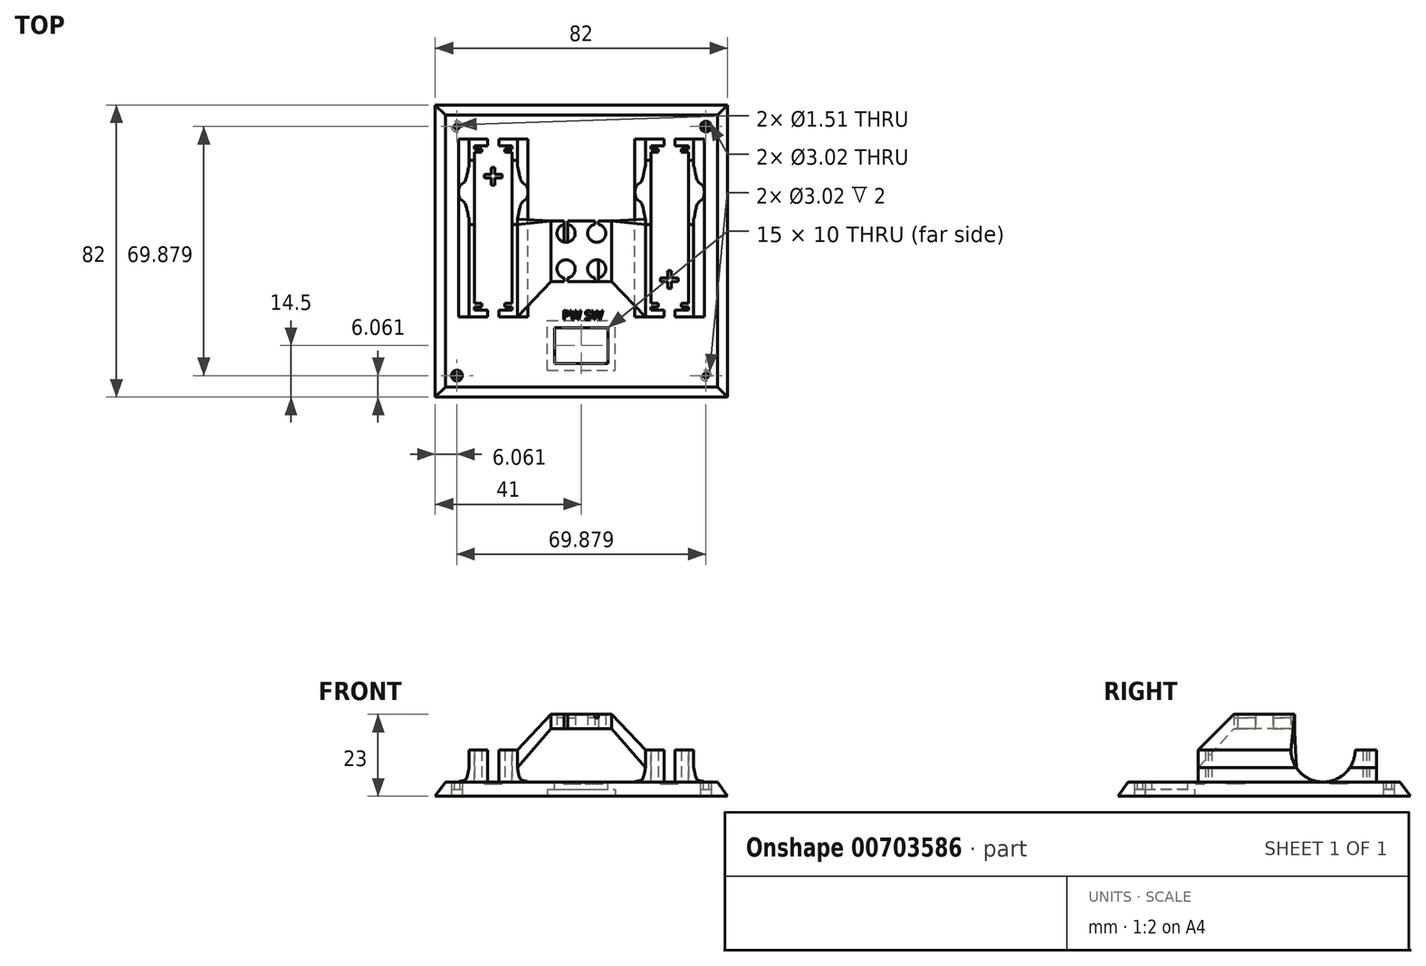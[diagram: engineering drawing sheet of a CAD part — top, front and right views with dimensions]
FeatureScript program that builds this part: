
annotation { "Feature Type Name" : "Feature", "Feature Type Description" : "" }
export const myFeature = defineFeature(function(context is Context, id is Id, definition is map)
    precondition{}
    {
        {
            assignVariable(context, id + "F0", {"name" : "Hollow", "anyValue" : 82});
        }
        {
            assignVariable(context, id + "F1", {"name" : "BaseThicknes", "anyValue" : 4});
        }
        {
            var Q0;
            Q0=qCreatedBy(makeId("Top.planeOp"),FACE);
            cPlane(context, id + "F2", {"entities" : qUnion([Q0]), "cplaneType" : CPlaneType.OFFSET, "offset" : (sqrt((sqrt((getVariable(context, 'Hollow') * getVariable(context, 'Hollow')) - ((getVariable(context, 'Hollow') / 2) * (getVariable(context, 'Hollow') / 2)))) * (sqrt((getVariable(context, 'Hollow') * getVariable(context, 'Hollow')) - ((getVariable(context, 'Hollow') / 2) * (getVariable(context, 'Hollow') / 2)))) - ((getVariable(context, 'Hollow') / 2) * (getVariable(context, 'Hollow') / 2)))) * mm, "width" : 150 * mm, "height" : 150 * mm});
        }
        {
            var Q0;
            Q0=qCreatedBy(id+"F2.planeOp",FACE);
            var sketch = newSketch(context, id + "F3", { "sketchPlane" : qUnion([Q0])});
            skPoint(sketch, "E0", {"position": v(0, 0) * mm});
            skSolve(sketch);
        }
        {
            var Q0;
            Q0=qCreatedBy(makeId("Top.planeOp"),FACE);
            var sketch = newSketch(context, id + "F4", { "sketchPlane" : qUnion([Q0])});
            skLineSegment(sketch, "E1.bottom", {"start": v(-41, 41) * mm, "end": v(41, 41) * mm});
            skLineSegment(sketch, "E1.top", {"start": v(-41, -41) * mm, "end": v(41, -41) * mm});
            skLineSegment(sketch, "E1.left", {"start": v(-41, 41) * mm, "end": v(-41, -41) * mm});
            skLineSegment(sketch, "E1.right", {"start": v(41, 41) * mm, "end": v(41, -41) * mm});
            skSolve(sketch);
        }
        {
            var Q0;
            Q0=qSketchRegion(id+"F4",true);
            extrude(context, id + "F5", {"entities" : qUnion([Q0]), "depth" : (getVariable(context, 'BaseThicknes')) * mm, "offsetDistance" : 25 * mm});
        }
        {
            var Q1;
            Q1=makeQuery(id+"F5.opExtrude","CAP_FACE",FACE,{"disambiguationData":[OSD([sQuery(id+"F4.wireOp",EDGE,"E1.bottom"),sQuery(id+"F4.wireOp",EDGE,"E1.top"),sQuery(id+"F4.wireOp",EDGE,"E1.left"),sQuery(id+"F4.wireOp",EDGE,"E1.right")])],"isStart":true});
            var Q2;
            Q2=sQuery(id+"F3.wireOp",VERTEX,"E0");
            loft(context, id + "F6", {"operationType" : NewBodyOperationType.INTERSECT, "sheetProfilesArray" : [{ "sheetProfileEntities" : qUnion([Q1]) }, { "sheetProfileEntities" : qUnion([Q2]) }]});
        }
        {
            var Q0;
            Q0=makeQuery(id+"F5.opExtrude","CAP_FACE",FACE,{"disambiguationData":[OSD([sQuery(id+"F4.wireOp",EDGE,"E1.bottom"),sQuery(id+"F4.wireOp",EDGE,"E1.top"),sQuery(id+"F4.wireOp",EDGE,"E1.left"),sQuery(id+"F4.wireOp",EDGE,"E1.right")])],"isStart":true});
            var sketch = newSketch(context, id + "F7", { "sketchPlane" : qUnion([Q0])});
            skCircle(sketch, "E2", {"center": v(-34.94, -34.94) * mm, "radius": 0.76 * mm});
            skCircle(sketch, "E3.MirrorC", {"center": v(34.94, -34.94) * mm, "radius": 0.76 * mm});
            skCircle(sketch, "E4.MirrorC", {"center": v(34.94, 34.94) * mm, "radius": 0.76 * mm});
            skCircle(sketch, "E5.MirrorC", {"center": v(-34.94, 34.94) * mm, "radius": 0.76 * mm});
            skCircle(sketch, "E6", {"center": v(-34.94, -34.94) * mm, "radius": 1.51 * mm});
            skCircle(sketch, "E7.MirrorC", {"center": v(-34.94, 34.94) * mm, "radius": 1.51 * mm});
            skCircle(sketch, "E8.MirrorC", {"center": v(34.94, -34.94) * mm, "radius": 1.51 * mm});
            skCircle(sketch, "E9.MirrorC", {"center": v(34.94, 34.94) * mm, "radius": 1.51 * mm});
            skSolve(sketch);
        }
        {
            var Q0;
            Q0=makeQuery(id+"F7.imprint","IMPRINT",FACE,{"disambiguationData":[TD([[makeQuery(id+"F7.imprint","IMPRINT",EDGE,{"derivedFrom":sQuery(id+"F7.wireOp",EDGE,"E2")}),1.0]])]});
            var Q1;
            Q1=makeQuery(id+"F7.imprint","IMPRINT",FACE,{"disambiguationData":[TD([[makeQuery(id+"F7.imprint","IMPRINT",EDGE,{"derivedFrom":sQuery(id+"F7.wireOp",EDGE,"E5.MirrorC")}),-1.0]])]});
            var Q2;
            Q2=makeQuery(id+"F7.imprint","IMPRINT",FACE,{"disambiguationData":[TD([[makeQuery(id+"F7.imprint","IMPRINT",EDGE,{"derivedFrom":sQuery(id+"F7.wireOp",EDGE,"E4.MirrorC")}),1.0]])]});
            var Q3;
            Q3=makeQuery(id+"F7.imprint","IMPRINT",FACE,{"disambiguationData":[TD([[makeQuery(id+"F7.imprint","IMPRINT",EDGE,{"derivedFrom":sQuery(id+"F7.wireOp",EDGE,"E3.MirrorC")}),-1.0]])]});
            extrude(context, id + "F8", {"entities" : qUnion([Q0, Q1, Q2, Q3]), "operationType" : NewBodyOperationType.REMOVE, "oppositeDirection" : true, "depth" : 25 * mm, "offsetDistance" : 25 * mm});
        }
        {
            var Q0;
            Q0=makeQuery(id+"F7.imprint","IMPRINT",FACE,{"disambiguationData":[TD([[makeQuery(id+"F7.imprint","IMPRINT",EDGE,{"derivedFrom":sQuery(id+"F7.wireOp",EDGE,"E5.MirrorC")}),1.0]])]});
            var Q1;
            Q1=makeQuery(id+"F7.imprint","IMPRINT",FACE,{"disambiguationData":[TD([[makeQuery(id+"F7.imprint","IMPRINT",EDGE,{"derivedFrom":sQuery(id+"F7.wireOp",EDGE,"E4.MirrorC")}),-1.0]])]});
            var Q2;
            Q2=makeQuery(id+"F7.imprint","IMPRINT",FACE,{"disambiguationData":[TD([[makeQuery(id+"F7.imprint","IMPRINT",EDGE,{"derivedFrom":sQuery(id+"F7.wireOp",EDGE,"E2")}),-1.0]])]});
            var Q3;
            Q3=makeQuery(id+"F7.imprint","IMPRINT",FACE,{"disambiguationData":[TD([[makeQuery(id+"F7.imprint","IMPRINT",EDGE,{"derivedFrom":sQuery(id+"F7.wireOp",EDGE,"E3.MirrorC")}),1.0]])]});
            extrude(context, id + "F9", {"entities" : qUnion([Q0, Q1, Q2, Q3]), "operationType" : NewBodyOperationType.REMOVE, "oppositeDirection" : true, "depth" : 2 * mm, "offsetDistance" : 25 * mm});
        }
        {
            var Q0;
            Q0=makeQuery(id+"F5.opExtrude","CAP_FACE",FACE,{"disambiguationData":[OSD([sQuery(id+"F4.wireOp",EDGE,"E1.bottom"),sQuery(id+"F4.wireOp",EDGE,"E1.top"),sQuery(id+"F4.wireOp",EDGE,"E1.left"),sQuery(id+"F4.wireOp",EDGE,"E1.right")])],"isStart":false});
            var sketch = newSketch(context, id + "F10", { "sketchPlane" : qUnion([Q0])});
            skLineSegment(sketch, "E10.bottom", {"start": v(-30, 29.5) * mm, "end": v(-26.3, 29.5) * mm});
            skLineSegment(sketch, "E10.top", {"start": v(-30, -16.5) * mm, "end": v(-26.3, -16.5) * mm});
            skLineSegment(sketch, "E10.left", {"start": v(-30, 29.5) * mm, "end": v(-30, -16.5) * mm});
            skLineSegment(sketch, "E10.right", {"start": v(-19.5, 29.5) * mm, "end": v(-19.5, -16.5) * mm});
            skLineSegment(sketch, "E11.bottom", {"start": v(-31.5, 31.5) * mm, "end": v(-26.3, 31.5) * mm});
            skLineSegment(sketch, "E11.top", {"start": v(-31.5, -18.5) * mm, "end": v(-18, -18.5) * mm});
            skLineSegment(sketch, "E11.left", {"start": v(-31.5, 31.5) * mm, "end": v(-31.5, -18.5) * mm});
            skLineSegment(sketch, "E11.right", {"start": v(-18, 31.5) * mm, "end": v(-18, -18.5) * mm});
            skLineSegment(sketch, "E12", {"start": v(-30, 27.7) * mm, "end": v(-28, 27.7) * mm});
            skLineSegment(sketch, "E13", {"start": v(-30, 28.7) * mm, "end": v(-28, 28.7) * mm});
            skLineSegment(sketch, "E14.left", {"start": v(-21.5, 28.7) * mm, "end": v(-21.5, 27.7) * mm});
            skLineSegment(sketch, "E14.right", {"start": v(-28, 28.7) * mm, "end": v(-28, 27.7) * mm});
            skLineSegment(sketch, "E15", {"start": v(-18, 6.5) * mm, "end": v(-31.5, 6.5) * mm, "construction": true});
            skLineSegment(sketch, "E16.trimOffspring", {"start": v(-21.5, 27.7) * mm, "end": v(-19.5, 27.7) * mm});
            skLineSegment(sketch, "E17.trimOffspring", {"start": v(-21.5, 28.7) * mm, "end": v(-19.5, 28.7) * mm});
            skLineSegment(sketch, "E18.MirrorCS", {"start": v(-30, -15.7) * mm, "end": v(-28, -15.7) * mm});
            skLineSegment(sketch, "E19.MirrorCS", {"start": v(-30, -14.7) * mm, "end": v(-28, -14.7) * mm});
            skLineSegment(sketch, "E20.MirrorCS", {"start": v(-21.5, -15.7) * mm, "end": v(-21.5, -14.7) * mm});
            skLineSegment(sketch, "E21.MirrorCS", {"start": v(-21.5, -15.7) * mm, "end": v(-19.5, -15.7) * mm});
            skLineSegment(sketch, "E22.MirrorCS", {"start": v(-21.5, -14.7) * mm, "end": v(-19.5, -14.7) * mm});
            skLineSegment(sketch, "E23.MirrorCS", {"start": v(-28, -15.7) * mm, "end": v(-28, -14.7) * mm});
            skLineSegment(sketch, "E24", {"start": v(-26.3, 31.5) * mm, "end": v(-26.3, 29.5) * mm});
            skLineSegment(sketch, "E25", {"start": v(-23.2, 31.5) * mm, "end": v(-23.2, 29.5) * mm});
            skLineSegment(sketch, "E26.trimOffspring", {"start": v(-23.2, 31.5) * mm, "end": v(-18, 31.5) * mm});
            skLineSegment(sketch, "E27.trimOffspring", {"start": v(-23.2, 29.5) * mm, "end": v(-19.5, 29.5) * mm});
            skLineSegment(sketch, "E28.MirrorCS", {"start": v(-26.3, -18.5) * mm, "end": v(-26.3, -16.5) * mm});
            skLineSegment(sketch, "E29.MirrorCS", {"start": v(-23.2, -18.5) * mm, "end": v(-23.2, -16.5) * mm});
            skLineSegment(sketch, "E30.trimOffspring", {"start": v(-23.2, -16.5) * mm, "end": v(-19.5, -16.5) * mm});
            skLineSegment(sketch, "E31.MirrorCS", {"start": v(21.5, 28.7) * mm, "end": v(21.5, 27.7) * mm});
            skLineSegment(sketch, "E32.MirrorCS", {"start": v(21.5, 28.7) * mm, "end": v(19.5, 28.7) * mm});
            skLineSegment(sketch, "E33.MirrorCS", {"start": v(23.2, 29.5) * mm, "end": v(19.5, 29.5) * mm});
            skLineSegment(sketch, "E34.MirrorCS", {"start": v(23.2, 31.5) * mm, "end": v(23.2, 29.5) * mm});
            skLineSegment(sketch, "E35.MirrorCS", {"start": v(28, -15.7) * mm, "end": v(28, -14.7) * mm});
            skLineSegment(sketch, "E36.MirrorCS", {"start": v(21.5, -15.7) * mm, "end": v(19.5, -15.7) * mm});
            skLineSegment(sketch, "E37.MirrorCS", {"start": v(23.2, -16.5) * mm, "end": v(19.5, -16.5) * mm});
            skLineSegment(sketch, "E38.MirrorCS", {"start": v(30, -15.7) * mm, "end": v(28, -15.7) * mm});
            skLineSegment(sketch, "E39.MirrorCS", {"start": v(21.5, -14.7) * mm, "end": v(19.5, -14.7) * mm});
            skLineSegment(sketch, "E40.MirrorCS", {"start": v(30, 29.5) * mm, "end": v(26.3, 29.5) * mm});
            skLineSegment(sketch, "E41.MirrorCS", {"start": v(30, 28.7) * mm, "end": v(28, 28.7) * mm});
            skLineSegment(sketch, "E42.MirrorCS", {"start": v(30, -16.5) * mm, "end": v(26.3, -16.5) * mm});
            skLineSegment(sketch, "E43.MirrorCS", {"start": v(26.3, 31.5) * mm, "end": v(26.3, 29.5) * mm});
            skLineSegment(sketch, "E44.MirrorCS", {"start": v(21.5, -15.7) * mm, "end": v(21.5, -14.7) * mm});
            skLineSegment(sketch, "E45.MirrorCS", {"start": v(28, 28.7) * mm, "end": v(28, 27.7) * mm});
            skLineSegment(sketch, "E46.MirrorCS", {"start": v(30, -14.7) * mm, "end": v(28, -14.7) * mm});
            skLineSegment(sketch, "E47.MirrorCS", {"start": v(31.5, 31.5) * mm, "end": v(26.3, 31.5) * mm});
            skLineSegment(sketch, "E48.MirrorCS", {"start": v(21.5, 27.7) * mm, "end": v(19.5, 27.7) * mm});
            skLineSegment(sketch, "E49.MirrorCS", {"start": v(23.2, -18.5) * mm, "end": v(23.2, -16.5) * mm});
            skLineSegment(sketch, "E50.MirrorCS", {"start": v(30, 27.7) * mm, "end": v(28, 27.7) * mm});
            skLineSegment(sketch, "E51.MirrorCS", {"start": v(26.3, -18.5) * mm, "end": v(26.3, -16.5) * mm});
            skLineSegment(sketch, "E52.MirrorCS", {"start": v(23.2, 31.5) * mm, "end": v(18, 31.5) * mm});
            skLineSegment(sketch, "E53.MirrorCS", {"start": v(31.5, 31.5) * mm, "end": v(31.5, -18.5) * mm});
            skLineSegment(sketch, "E54.MirrorCS", {"start": v(30, 29.5) * mm, "end": v(30, -16.5) * mm});
            skLineSegment(sketch, "E55.MirrorCS", {"start": v(31.5, -18.5) * mm, "end": v(18, -18.5) * mm});
            skLineSegment(sketch, "E56.MirrorCS", {"start": v(19.5, 29.5) * mm, "end": v(19.5, -16.5) * mm});
            skLineSegment(sketch, "E57.MirrorCS", {"start": v(18, 31.5) * mm, "end": v(18, -18.5) * mm});
            skLineSegment(sketch, "E58.MirrorCS", {"start": v(18, 6.5) * mm, "end": v(31.5, 6.5) * mm, "construction": true});
            skSolve(sketch);
        }
        {
            var Q0;
            {var subQ5=sQuery(id+"F10.wireOp",EDGE,"E33.MirrorCS");Q0=makeQuery(id+"F10.imprint","IMPRINT",FACE,{"disambiguationData":[TD([[makeQuery(id+"F10.imprint","IMPRINT",EDGE,{"derivedFrom":subQ5}),-1.0]])]});}
            var Q1;
            {var subQ6=sQuery(id+"F10.wireOp",EDGE,"E40.MirrorCS");Q1=makeQuery(id+"F10.imprint","IMPRINT",FACE,{"disambiguationData":[TD([[makeQuery(id+"F10.imprint","IMPRINT",EDGE,{"derivedFrom":subQ6}),-1.0]])]});}
            var Q2;
            Q2=makeQuery(id+"F10.imprint","IMPRINT",FACE,{"disambiguationData":[TD([[makeQuery(id+"F10.imprint","IMPRINT",EDGE,{"derivedFrom":sQuery(id+"F10.wireOp",EDGE,"E31.MirrorCS")}),-1.0]])]});
            var Q3;
            {var subQ0=sQuery(id+"F10.wireOp",EDGE,"E41.MirrorCS");Q3=makeQuery(id+"F10.imprint","IMPRINT",FACE,{"disambiguationData":[TD([[makeQuery(id+"F10.imprint","IMPRINT",EDGE,{"derivedFrom":subQ0}),1.0]])]});}
            var Q4;
            {var subQ0=sQuery(id+"F10.wireOp",EDGE,"E36.MirrorCS");Q4=makeQuery(id+"F10.imprint","IMPRINT",FACE,{"disambiguationData":[TD([[makeQuery(id+"F10.imprint","IMPRINT",EDGE,{"derivedFrom":subQ0}),-1.0]])]});}
            var Q5;
            Q5=makeQuery(id+"F10.imprint","IMPRINT",FACE,{"disambiguationData":[TD([[makeQuery(id+"F10.imprint","IMPRINT",EDGE,{"derivedFrom":sQuery(id+"F10.wireOp",EDGE,"E35.MirrorCS")}),-1.0]])]});
            var Q6;
            Q6=makeQuery(id+"F10.imprint","IMPRINT",FACE,{"disambiguationData":[TD([[makeQuery(id+"F10.imprint","IMPRINT",EDGE,{"derivedFrom":sQuery(id+"F10.wireOp",EDGE,"E20.MirrorCS")}),-1.0]])]});
            var Q7;
            {var subQ0=sQuery(id+"F10.wireOp",EDGE,"E18.MirrorCS");Q7=makeQuery(id+"F10.imprint","IMPRINT",FACE,{"disambiguationData":[TD([[makeQuery(id+"F10.imprint","IMPRINT",EDGE,{"derivedFrom":subQ0}),1.0]])]});}
            var Q8;
            {var subQ6=sQuery(id+"F10.wireOp",EDGE,"E10.bottom");Q8=makeQuery(id+"F10.imprint","IMPRINT",FACE,{"disambiguationData":[TD([[makeQuery(id+"F10.imprint","IMPRINT",EDGE,{"derivedFrom":subQ6}),1.0]])]});}
            var Q9;
            {var subQ0=sQuery(id+"F10.wireOp",EDGE,"E11.right");Q9=makeQuery(id+"F10.imprint","IMPRINT",FACE,{"disambiguationData":[TD([[makeQuery(id+"F10.imprint","IMPRINT",EDGE,{"derivedFrom":subQ0}),-1.0]])]});}
            var Q10;
            {var subQ0=sQuery(id+"F10.wireOp",EDGE,"E12");Q10=makeQuery(id+"F10.imprint","IMPRINT",FACE,{"disambiguationData":[TD([[makeQuery(id+"F10.imprint","IMPRINT",EDGE,{"derivedFrom":subQ0}),1.0]])]});}
            var Q11;
            Q11=makeQuery(id+"F10.imprint","IMPRINT",FACE,{"disambiguationData":[TD([[makeQuery(id+"F10.imprint","IMPRINT",EDGE,{"derivedFrom":sQuery(id+"F10.wireOp",EDGE,"E14.left")}),1.0]])]});
            extrude(context, id + "F11", {"entities" : qUnion([Q0, Q1, Q2, Q3, Q4, Q5, Q6, Q7, Q8, Q9, Q10, Q11]), "operationType" : NewBodyOperationType.ADD, "depth" : 9 * mm, "offsetDistance" : 25 * mm});
        }
        {
            var Q0;
            Q0=qCreatedBy(makeId("Front.planeOp"),FACE);
            var sketch = newSketch(context, id + "F12", { "sketchPlane" : qUnion([Q0])});
            skLineSegment(sketch, "E59", {"start": v(-31.5, 4) * mm, "end": v(-34.5, 4) * mm});
            skLineSegment(sketch, "E60", {"start": v(-31.5, 4) * mm, "end": v(-31.5, 8) * mm});
            skPoint(sketch, "E61", {"position": v(-34.5, 4) * mm});
            skFitSpline(sketch, "E62", {"points": [v(-31.5, 8) * mm, v(-32.53, 4.65) * mm, v(-34.5, 4) * mm], "startDerivative": vector(-1.67, -5.36) * mm, "endDerivative": vector(-4.69, -2.88) * mm});
            skLineSegment(sketch, "E63", {"start": v(-24.75, 13.95) * mm, "end": v(-24.75, 2.35) * mm, "construction": true});
            skFitSpline(sketch, "E64.MirrorCS", {"points": [v(-18, 8) * mm, v(-16.97, 4.65) * mm, v(-15, 4) * mm], "startDerivative": vector(1.67, -5.36) * mm, "endDerivative": vector(4.69, -2.88) * mm});
            skFitSpline(sketch, "E65.MirrorCS", {"points": [v(18, 8) * mm, v(16.97, 4.65) * mm, v(15, 4) * mm], "startDerivative": vector(-1.67, -5.36) * mm, "endDerivative": vector(-4.69, -2.88) * mm});
            skFitSpline(sketch, "E66.MirrorCS", {"points": [v(31.5, 8) * mm, v(32.53, 4.65) * mm, v(34.5, 4) * mm], "startDerivative": vector(1.67, -5.36) * mm, "endDerivative": vector(4.69, -2.88) * mm});
            skLineSegment(sketch, "E67.MirrorCS", {"start": v(-18, 4) * mm, "end": v(-15, 4) * mm});
            skLineSegment(sketch, "E68.MirrorCS", {"start": v(18, 4) * mm, "end": v(15, 4) * mm});
            skLineSegment(sketch, "E69.MirrorCS", {"start": v(31.5, 4) * mm, "end": v(34.5, 4) * mm});
            skLineSegment(sketch, "E70.MirrorCS", {"start": v(-18, 4) * mm, "end": v(-18, 8) * mm});
            skLineSegment(sketch, "E71.MirrorCS", {"start": v(18, 4) * mm, "end": v(18, 8) * mm});
            skLineSegment(sketch, "E72.MirrorCS", {"start": v(31.5, 4) * mm, "end": v(31.5, 8) * mm});
            skSolve(sketch);
        }
        {
            var Q0;
            Q0=qSketchRegion(id+"F12",true);
            extrude(context, id + "F13", {"entities" : qUnion([Q0]), "operationType" : NewBodyOperationType.ADD, "depth" : 18.5 * mm, "offsetDistance" : 25 * mm, "hasSecondDirection" : true, "secondDirectionOppositeDirection" : true, "secondDirectionDepth" : 31.5 * mm});
        }
        {
            var Q0;
            Q0=qCreatedBy(makeId("Right.planeOp"),FACE);
            var sketch = newSketch(context, id + "F14", { "sketchPlane" : qUnion([Q0])});
            skCircle(sketch, "E73", {"center": v(16.5, 13) * mm, "radius": 9 * mm});
            skCircle(sketch, "E74", {"center": v(-3.5, 13) * mm, "radius": 9 * mm});
            skSolve(sketch);
        }
        {
            var Q0;
            Q0=makeQuery(id+"F14.imprint","IMPRINT",FACE,{"disambiguationData":[TD([[makeQuery(id+"F14.imprint","IMPRINT",EDGE,{"derivedFrom":sQuery(id+"F14.wireOp",EDGE,"E73")}),1.0]])]});
            extrude(context, id + "F15", {"entities" : qUnion([Q0]), "operationType" : NewBodyOperationType.REMOVE, "oppositeDirection" : true, "depth" : 50 * mm, "offsetDistance" : 25 * mm, "hasSecondDirection" : true, "secondDirectionOppositeDirection" : false, "secondDirectionDepth" : 52.3 * mm});
        }
        {
            var Q0;
            Q0=makeQuery(id+"F5.opExtrude","CAP_FACE",FACE,{"disambiguationData":[OSD([sQuery(id+"F4.wireOp",EDGE,"E1.bottom"),sQuery(id+"F4.wireOp",EDGE,"E1.top"),sQuery(id+"F4.wireOp",EDGE,"E1.left"),sQuery(id+"F4.wireOp",EDGE,"E1.right")])],"isStart":false});
            var sketch = newSketch(context, id + "F16", { "sketchPlane" : qUnion([Q0])});
            skLineSegment(sketch, "E75.bottom", {"start": v(-7.5, -21.5) * mm, "end": v(7.5, -21.5) * mm});
            skLineSegment(sketch, "E75.top", {"start": v(-7.5, -31.5) * mm, "end": v(7.5, -31.5) * mm});
            skLineSegment(sketch, "E75.left", {"start": v(-7.5, -21.5) * mm, "end": v(-7.5, -31.5) * mm});
            skLineSegment(sketch, "E75.right", {"start": v(7.5, -21.5) * mm, "end": v(7.5, -31.5) * mm});
            skSolve(sketch);
        }
        {
            var Q0;
            Q0=qSketchRegion(id+"F16",true);
            extrude(context, id + "F17", {"entities" : qUnion([Q0]), "operationType" : NewBodyOperationType.REMOVE, "oppositeDirection" : true, "depth" : 25 * mm, "offsetDistance" : 25 * mm});
        }
        {
            var Q0;
            Q0=makeQuery(id+"F5.opExtrude","CAP_FACE",FACE,{"disambiguationData":[OSD([sQuery(id+"F4.wireOp",EDGE,"E1.bottom"),sQuery(id+"F4.wireOp",EDGE,"E1.top"),sQuery(id+"F4.wireOp",EDGE,"E1.left"),sQuery(id+"F4.wireOp",EDGE,"E1.right")])],"isStart":true});
            var sketch = newSketch(context, id + "F18", { "sketchPlane" : qUnion([Q0])});
            skLineSegment(sketch, "E76.bottom", {"start": v(-9.5, 33.5) * mm, "end": v(9.5, 33.5) * mm});
            skLineSegment(sketch, "E76.top", {"start": v(-9.5, 19.5) * mm, "end": v(9.5, 19.5) * mm});
            skLineSegment(sketch, "E76.left", {"start": v(-9.5, 33.5) * mm, "end": v(-9.5, 19.5) * mm});
            skLineSegment(sketch, "E76.right", {"start": v(9.5, 33.5) * mm, "end": v(9.5, 19.5) * mm});
            skSolve(sketch);
        }
        {
            var Q0;
            Q0=qSketchRegion(id+"F18",true);
            extrude(context, id + "F19", {"entities" : qUnion([Q0]), "operationType" : NewBodyOperationType.REMOVE, "oppositeDirection" : true, "depth" : 2 * mm, "offsetDistance" : 25 * mm});
        }
        {
            var Q0;
            Q0=makeQuery(id+"F5.opExtrude","CAP_FACE",FACE,{"disambiguationData":[OSD([sQuery(id+"F4.wireOp",EDGE,"E1.bottom"),sQuery(id+"F4.wireOp",EDGE,"E1.top"),sQuery(id+"F4.wireOp",EDGE,"E1.left"),sQuery(id+"F4.wireOp",EDGE,"E1.right")])],"isStart":false});
            var sketch = newSketch(context, id + "F20", { "sketchPlane" : qUnion([Q0])});
            skLineSegment(sketch, "E77.bottom", {"start": v(-25.25, 23.5) * mm, "end": v(-24.25, 23.5) * mm});
            skLineSegment(sketch, "E77.top", {"start": v(-25.25, 18.5) * mm, "end": v(-24.25, 18.5) * mm});
            skLineSegment(sketch, "E77.left", {"start": v(-25.25, 23.5) * mm, "end": v(-25.25, 18.5) * mm});
            skLineSegment(sketch, "E77.right", {"start": v(-24.25, 23.5) * mm, "end": v(-24.25, 18.5) * mm});
            skLineSegment(sketch, "E78.bottom", {"start": v(-27.25, 21.5) * mm, "end": v(-22.25, 21.5) * mm});
            skLineSegment(sketch, "E78.top", {"start": v(-27.25, 20.5) * mm, "end": v(-22.25, 20.5) * mm});
            skLineSegment(sketch, "E78.left", {"start": v(-27.25, 21.5) * mm, "end": v(-27.25, 20.5) * mm});
            skLineSegment(sketch, "E78.right", {"start": v(-22.25, 21.5) * mm, "end": v(-22.25, 20.5) * mm});
            skLineSegment(sketch, "E79", {"start": v(-24.75, 32.18) * mm, "end": v(-24.75, -20.77) * mm, "construction": true});
            skLineSegment(sketch, "E80.bottom", {"start": v(24.2, -5.5) * mm, "end": v(25.2, -5.5) * mm});
            skLineSegment(sketch, "E80.top", {"start": v(24.2, -10.5) * mm, "end": v(25.2, -10.5) * mm});
            skLineSegment(sketch, "E80.left", {"start": v(24.2, -5.5) * mm, "end": v(24.2, -10.5) * mm});
            skLineSegment(sketch, "E80.right", {"start": v(25.2, -5.5) * mm, "end": v(25.2, -10.5) * mm});
            skLineSegment(sketch, "E81.bottom", {"start": v(22.2, -7.5) * mm, "end": v(27.2, -7.5) * mm});
            skLineSegment(sketch, "E81.top", {"start": v(22.2, -8.5) * mm, "end": v(27.2, -8.5) * mm});
            skLineSegment(sketch, "E81.left", {"start": v(22.2, -7.5) * mm, "end": v(22.2, -8.5) * mm});
            skLineSegment(sketch, "E81.right", {"start": v(27.2, -7.5) * mm, "end": v(27.2, -8.5) * mm});
            skLineSegment(sketch, "E82", {"start": v(24.7, 5.1) * mm, "end": v(24.7, -19.14) * mm, "construction": true});
            skText(sketch, "E83", { "text": "PW SW", "fontName": "OpenSans-Regular.ttf"});
            const initialGuessF20  = {"E83": [-0.00532, -0.01924, 1, 0, 0.00251]};
            skSetInitialGuess(sketch, initialGuessF20);
            skSolve(sketch);
        }
        {
            var Q0;
            Q0=qSketchRegion(id+"F20",true);
            extrude(context, id + "F21", {"entities" : qUnion([Q0]), "operationType" : NewBodyOperationType.REMOVE, "oppositeDirection" : true, "depth" : .5 * mm, "offsetDistance" : 25 * mm});
        }
        {
            var Q0;
            Q0=makeQuery(id+"F20.imprint","IMPRINT",FACE,{"disambiguationData":[TD([[makeQuery(id+"F20.imprint","IMPRINT",EDGE,{"derivedFrom":sQuery(id+"F20.wireOp",EDGE,"E83.sketch_text.stroke-35")}),-1.0]])]});
            var Q1;
            Q1=makeQuery(id+"F20.imprint","IMPRINT",FACE,{"disambiguationData":[TD([[makeQuery(id+"F20.imprint","IMPRINT",EDGE,{"derivedFrom":sQuery(id+"F20.wireOp",EDGE,"E83.sketch_text.stroke-60")}),-1.0]])]});
            var Q2;
            Q2=makeQuery(id+"F20.imprint","IMPRINT",FACE,{"disambiguationData":[TD([[makeQuery(id+"F20.imprint","IMPRINT",EDGE,{"derivedFrom":sQuery(id+"F20.wireOp",EDGE,"E83.sketch_text.stroke-15")}),-1.0]])]});
            var Q3;
            Q3=makeQuery(id+"F20.imprint","IMPRINT",FACE,{"disambiguationData":[TD([[makeQuery(id+"F20.imprint","IMPRINT",EDGE,{"derivedFrom":sQuery(id+"F20.wireOp",EDGE,"E83.sketch_text.stroke-0")}),-1.0]])]});
            extrude(context, id + "F22", {"entities" : qUnion([Q0, Q1, Q2, Q3]), "operationType" : NewBodyOperationType.REMOVE, "oppositeDirection" : true, "depth" : .5 * mm, "offsetDistance" : 25 * mm});
        }
        {
            var Q0;
            {var subQ15=sQuery(id+"F4.wireOp",EDGE,"E1.right");var subQ16=sQuery(id+"F4.wireOp",EDGE,"E1.left");var subQ17=sQuery(id+"F4.wireOp",EDGE,"E1.top");var subQ18=sQuery(id+"F4.wireOp",EDGE,"E1.bottom");var subQ19=makeQuery(id+"F5.opExtrude","CAP_FACE",FACE,{"disambiguationData":[OSD([subQ18,subQ17,subQ16,subQ15])],"isStart":false});Q0=makeQuery(id+"F21.boolean.opBoolean","SPLIT",FACE,{"disambiguationData":[TD([makeQuery(id+"F8.boolean.opBoolean","COPY",FACE,{"derivedFrom":makeQuery(id+"F8.opExtrude","SWEPT_FACE",FACE,{"disambiguationData":[OSD([sQuery(id+"F7.wireOp",EDGE,"E2")])]})})])],"derivedFrom":subQ19});}
            cPlane(context, id + "F23", {"entities" : qUnion([Q0]), "cplaneType" : CPlaneType.OFFSET, "offset" : 15 * mm, "width" : 150 * mm, "height" : 150 * mm});
        }
        {
            var Q0;
            Q0=qCreatedBy(id+"F23.planeOp",FACE);
            var sketch = newSketch(context, id + "F24", { "sketchPlane" : qUnion([Q0])});
            skLineSegment(sketch, "E84.bottom", {"start": v(-8.5, 8.5) * mm, "end": v(-4.8, 8.5) * mm});
            skLineSegment(sketch, "E84.top", {"start": v(-8.5, -8.5) * mm, "end": v(8.5, -8.5) * mm});
            skLineSegment(sketch, "E84.left", {"start": v(-8.5, 8.5) * mm, "end": v(-8.5, -8.5) * mm});
            skLineSegment(sketch, "E84.right", {"start": v(8.5, 8.5) * mm, "end": v(8.5, -8.5) * mm});
            skArc(sketch, "E85", {"start": v(-4.8, 7.5) * mm, "mid": v(-4.3, 2.45) * mm, "end": v(-3.8, 7.5) * mm});
            skLineSegment(sketch, "E86.left", {"start": v(-4.8, 8.5) * mm, "end": v(-4.8, 2.5) * mm});
            skLineSegment(sketch, "E86.right", {"start": v(-3.8, 8.5) * mm, "end": v(-3.8, 2.5) * mm});
            skLineSegment(sketch, "E87.trimOffspring", {"start": v(-3.8, 8.5) * mm, "end": v(8.5, 8.5) * mm});
            skArc(sketch, "E88.MirrorCS", {"start": v(4.8, 7.5) * mm, "mid": v(4.3, 2.45) * mm, "end": v(3.8, 7.5) * mm});
            skLineSegment(sketch, "E89.MirrorCS", {"start": v(4.8, 8.5) * mm, "end": v(4.8, 2.5) * mm});
            skLineSegment(sketch, "E90.MirrorCS", {"start": v(3.8, 8.5) * mm, "end": v(3.8, 2.5) * mm});
            skArc(sketch, "E91.MirrorCS", {"start": v(4.8, -7.5) * mm, "mid": v(4.3, -2.45) * mm, "end": v(3.8, -7.5) * mm});
            skLineSegment(sketch, "E92.MirrorCS", {"start": v(4.8, -8.5) * mm, "end": v(4.8, -2.5) * mm});
            skLineSegment(sketch, "E93.MirrorCS", {"start": v(3.8, -8.5) * mm, "end": v(3.8, -2.5) * mm});
            skArc(sketch, "E94.MirrorCS", {"start": v(-4.8, -7.5) * mm, "mid": v(-4.3, -2.45) * mm, "end": v(-3.8, -7.5) * mm});
            skLineSegment(sketch, "E95.MirrorCS", {"start": v(-4.8, -8.5) * mm, "end": v(-4.8, -2.5) * mm});
            skLineSegment(sketch, "E96.MirrorCS", {"start": v(-3.8, -8.5) * mm, "end": v(-3.8, -2.5) * mm});
            skSolve(sketch);
        }
        {
            var Q0;
            Q0=makeQuery(id+"F24.imprint","IMPRINT",FACE,{"disambiguationData":[TD([[makeQuery(id+"F24.imprint","IMPRINT",EDGE,{"derivedFrom":sQuery(id+"F24.wireOp",EDGE,"E84.bottom")}),-1.0]])]});
            extrude(context, id + "F25", {"entities" : qUnion([Q0]), "depth" : 4 * mm, "offsetDistance" : 25 * mm});
        }
        {
            var Q0;
            {var subQ1=sQuery(id+"F10.wireOp",EDGE,"E11.right");var subQ2=sQuery(id+"F10.wireOp",EDGE,"E11.top");Q0=makeQuery(id+"F15.boolean.opBoolean","SPLIT",FACE,{"disambiguationData":[TD([makeQuery(id+"F11.opExtrude","SWEPT_FACE",FACE,{"disambiguationData":[OSD([subQ2]),TDD([makeQuery(id+"F10.imprint","IMPRINT",EDGE,{"disambiguationData":[TD([[makeQuery(id+"F10.imprint","INTERSECT",VERTEX,{"derivedFrom":[subQ2,subQ1]}),1.0]])],"derivedFrom":subQ2})])]})])],"derivedFrom":makeQuery(id+"F11.opExtrude","SWEPT_FACE",FACE,{"disambiguationData":[OSD([subQ1])]})});}
            var Q1;
            Q1=makeQuery(id+"F25.opExtrude","SWEPT_FACE",FACE,{"disambiguationData":[OSD([sQuery(id+"F24.wireOp",EDGE,"E84.left")])]});
            loft(context, id + "F26", {"sheetProfilesArray" : [{ "sheetProfileEntities" : qUnion([Q0]) }, { "sheetProfileEntities" : qUnion([Q1]) }]});
        }
        {
            var Q0;
            {var subQ1=sQuery(id+"F10.wireOp",EDGE,"E55.MirrorCS");var subQ2=sQuery(id+"F10.wireOp",EDGE,"E49.MirrorCS");var subQ3=sQuery(id+"F10.wireOp",EDGE,"E57.MirrorCS");Q0=makeQuery(id+"F15.boolean.opBoolean","SPLIT",FACE,{"disambiguationData":[TD([makeQuery(id+"F11.opExtrude","SWEPT_FACE",FACE,{"disambiguationData":[OSD([subQ1]),TDD([makeQuery(id+"F10.imprint","IMPRINT",EDGE,{"disambiguationData":[TD([[makeQuery(id+"F10.imprint","INTERSECT",VERTEX,{"derivedFrom":[subQ2,subQ1]}),-1.0]])],"derivedFrom":subQ1})])]})])],"derivedFrom":makeQuery(id+"F11.opExtrude","SWEPT_FACE",FACE,{"disambiguationData":[OSD([subQ3])]})});}
            var Q1;
            Q1=makeQuery(id+"F25.opExtrude","SWEPT_FACE",FACE,{"disambiguationData":[OSD([sQuery(id+"F24.wireOp",EDGE,"E84.right")])]});
            loft(context, id + "F27", {"sheetProfilesArray" : [{ "sheetProfileEntities" : qUnion([Q0]) }, { "sheetProfileEntities" : qUnion([Q1]) }]});
        }
        {
            var Q0;
            {var subQ0=sQuery(id+"F24.wireOp",EDGE,"E86.right");var subQ1=sQuery(id+"F24.wireOp",EDGE,"E85");var subQ2=makeQuery(id+"F24.imprint","INTERSECT",VERTEX,{"disambiguationData":[OD(0.0)],"derivedFrom":[subQ1,subQ0]});Q0=makeQuery(id+"F24.imprint","IMPRINT",FACE,{"disambiguationData":[TD([[makeQuery(id+"F24.imprint","IMPRINT",EDGE,{"disambiguationData":[TD([[subQ2,1.0]])],"derivedFrom":subQ1}),1.0]])]});}
            var Q1;
            {var subQ0=sQuery(id+"F24.wireOp",EDGE,"E86.left");var subQ1=sQuery(id+"F24.wireOp",EDGE,"E85");var subQ2=makeQuery(id+"F24.imprint","INTERSECT",VERTEX,{"disambiguationData":[OD(0.0)],"derivedFrom":[subQ1,subQ0]});Q1=makeQuery(id+"F24.imprint","IMPRINT",FACE,{"disambiguationData":[TD([[makeQuery(id+"F24.imprint","IMPRINT",EDGE,{"disambiguationData":[TD([[subQ2,-1.0]])],"derivedFrom":subQ1}),1.0]])]});}
            var Q2;
            {var subQ0=sQuery(id+"F24.wireOp",EDGE,"E90.MirrorCS");var subQ1=sQuery(id+"F24.wireOp",EDGE,"E88.MirrorCS");var subQ2=makeQuery(id+"F24.imprint","INTERSECT",VERTEX,{"disambiguationData":[OD(0.0)],"derivedFrom":[subQ1,subQ0]});Q2=makeQuery(id+"F24.imprint","IMPRINT",FACE,{"disambiguationData":[TD([[makeQuery(id+"F24.imprint","IMPRINT",EDGE,{"disambiguationData":[TD([[subQ2,1.0]])],"derivedFrom":subQ1}),-1.0]])]});}
            var Q3;
            {var subQ0=sQuery(id+"F24.wireOp",EDGE,"E89.MirrorCS");var subQ1=sQuery(id+"F24.wireOp",EDGE,"E88.MirrorCS");var subQ2=makeQuery(id+"F24.imprint","INTERSECT",VERTEX,{"disambiguationData":[OD(0.0)],"derivedFrom":[subQ1,subQ0]});Q3=makeQuery(id+"F24.imprint","IMPRINT",FACE,{"disambiguationData":[TD([[makeQuery(id+"F24.imprint","IMPRINT",EDGE,{"disambiguationData":[TD([[subQ2,-1.0]])],"derivedFrom":subQ1}),-1.0]])]});}
            var Q4;
            {var subQ0=sQuery(id+"F24.wireOp",EDGE,"E93.MirrorCS");var subQ1=sQuery(id+"F24.wireOp",EDGE,"E91.MirrorCS");var subQ2=makeQuery(id+"F24.imprint","INTERSECT",VERTEX,{"disambiguationData":[OD(0.0)],"derivedFrom":[subQ1,subQ0]});Q4=makeQuery(id+"F24.imprint","IMPRINT",FACE,{"disambiguationData":[TD([[makeQuery(id+"F24.imprint","IMPRINT",EDGE,{"disambiguationData":[TD([[subQ2,1.0]])],"derivedFrom":subQ1}),1.0]])]});}
            var Q5;
            {var subQ0=sQuery(id+"F24.wireOp",EDGE,"E92.MirrorCS");var subQ1=sQuery(id+"F24.wireOp",EDGE,"E91.MirrorCS");var subQ2=makeQuery(id+"F24.imprint","INTERSECT",VERTEX,{"disambiguationData":[OD(0.0)],"derivedFrom":[subQ1,subQ0]});Q5=makeQuery(id+"F24.imprint","IMPRINT",FACE,{"disambiguationData":[TD([[makeQuery(id+"F24.imprint","IMPRINT",EDGE,{"disambiguationData":[TD([[subQ2,-1.0]])],"derivedFrom":subQ1}),1.0]])]});}
            var Q6;
            {var subQ0=sQuery(id+"F24.wireOp",EDGE,"E95.MirrorCS");var subQ1=sQuery(id+"F24.wireOp",EDGE,"E94.MirrorCS");var subQ2=makeQuery(id+"F24.imprint","INTERSECT",VERTEX,{"disambiguationData":[OD(0.0)],"derivedFrom":[subQ1,subQ0]});Q6=makeQuery(id+"F24.imprint","IMPRINT",FACE,{"disambiguationData":[TD([[makeQuery(id+"F24.imprint","IMPRINT",EDGE,{"disambiguationData":[TD([[subQ2,-1.0]])],"derivedFrom":subQ1}),-1.0]])]});}
            var Q7;
            {var subQ0=sQuery(id+"F24.wireOp",EDGE,"E96.MirrorCS");var subQ1=sQuery(id+"F24.wireOp",EDGE,"E94.MirrorCS");var subQ2=makeQuery(id+"F24.imprint","INTERSECT",VERTEX,{"disambiguationData":[OD(0.0)],"derivedFrom":[subQ1,subQ0]});Q7=makeQuery(id+"F24.imprint","IMPRINT",FACE,{"disambiguationData":[TD([[makeQuery(id+"F24.imprint","IMPRINT",EDGE,{"disambiguationData":[TD([[subQ2,1.0]])],"derivedFrom":subQ1}),-1.0]])]});}
            extrude(context, id + "F28", {"entities" : qUnion([Q0, Q1, Q2, Q3, Q4, Q5, Q6, Q7]), "operationType" : NewBodyOperationType.ADD, "depth" : 3 * mm, "offsetDistance" : 25 * mm});
        }
    });
